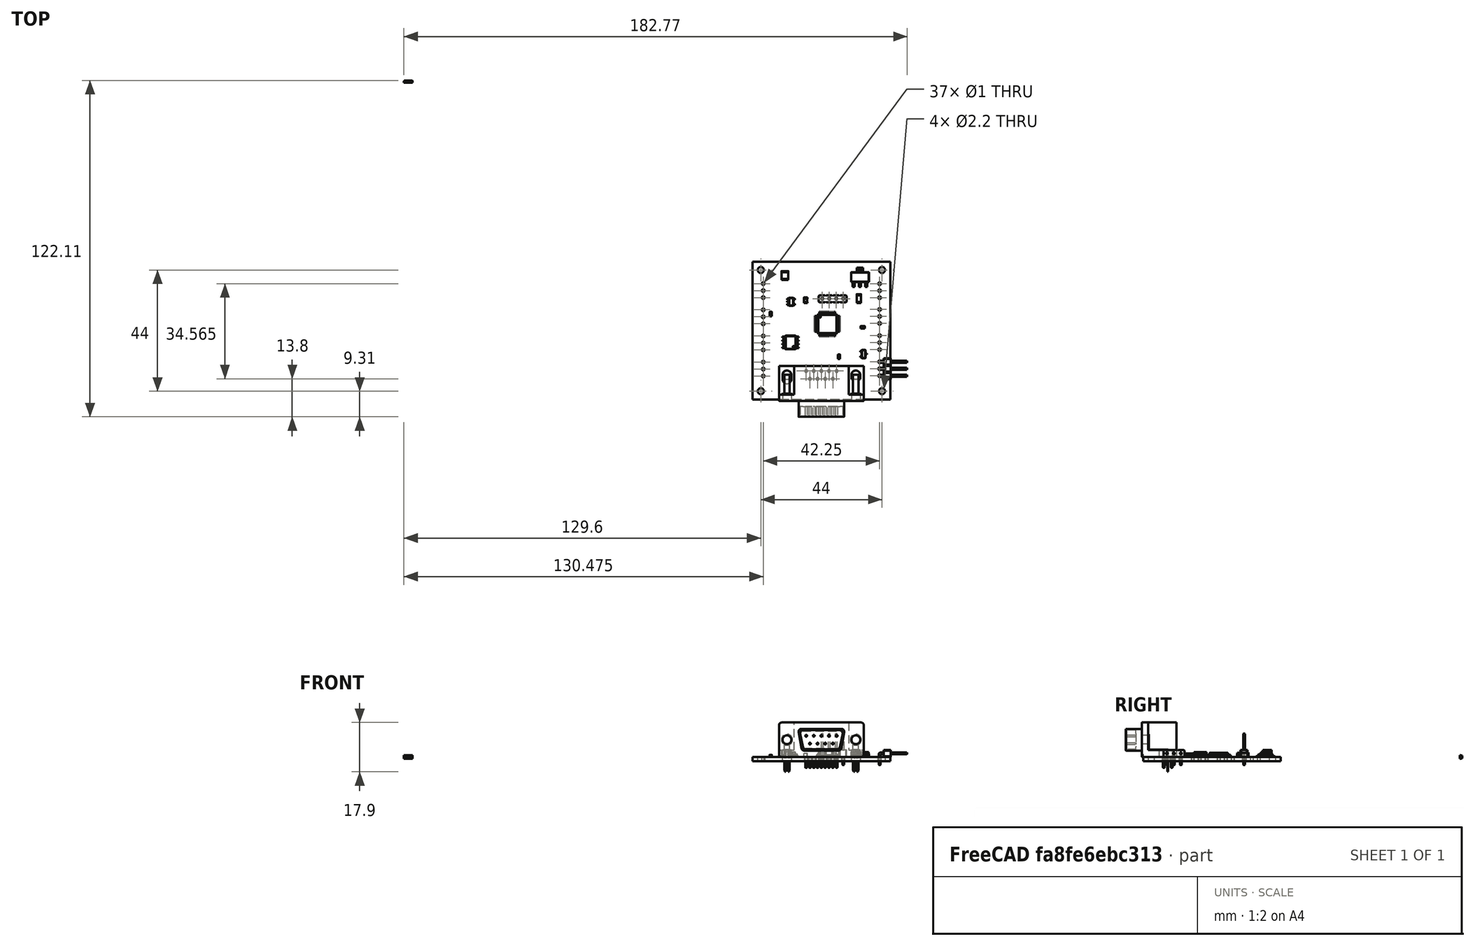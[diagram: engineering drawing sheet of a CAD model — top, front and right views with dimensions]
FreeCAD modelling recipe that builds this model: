
FCSTD DOCUMENT  (FreeCAD 0.20R29603 (Git))
Label: DGT-01
License: All rights reserved
LicenseURL: http://en.wikipedia.org/wiki/All_rights_reserved
objects: App::Link×55, Part::Feature×30, App::Part×6, PartDesign::CoordinateSystem×1, Sketcher::SketchObject×1
note: 32 computed .brp shape members not serialized (recipe doc carries the construction recipe); baked Part::Feature solids carry a one-line shape summary decoded from their .brp

FEATURE [PartDesign::CoordinateSystem] Local_CS_42b7
  AttacherType = Attacher::AttachEngine3D
  MapMode = 2
  Support = -> [X_Axis001]
FEATURE [Part::Feature] Pcb_42b7
  shape: bbox 50 x 50 x 1.6 mm, 49 faces (baked)
FEATURE [Sketcher::SketchObject] PCB_Sketch_42b7
  FullyConstrained = false
  sketch-geometry (4):
    g0: LineSegment StartX=125 StartY=-65.045 StartZ=0 EndX=175 EndY=-65.045 EndZ=0
    g1: LineSegment StartX=175 StartY=-65.045 StartZ=0 EndX=175 EndY=-115.045 EndZ=0
    g2: LineSegment StartX=175 StartY=-115.045 StartZ=0 EndX=125 EndY=-115.045 EndZ=0
    g3: LineSegment StartX=125 StartY=-115.045 StartZ=0 EndX=125 EndY=-65.045 EndZ=0
  constraints (4):
    c: Coincident(g2,g3)
    c: Coincident(g0,g3)
    c: Coincident(g1,g2)
    c: Coincident(g0,g1)
FEATURE [Part::Feature] Shape  label="R19_R_0603_1608Metric_04b1a8448a37"
  Placement = pos=(165,-88.8,0) rot=(0,0,1;0rad)
  shape: bbox 1.6 x 0.8 x 0.45 mm, 26 faces (baked)
FEATURE [Part::Feature] Shape001  label="C23_C_0603_1608Metric_67e658bcb3e9"
  Placement = pos=(131.6,-84,0) rot=(0,0,1;1.5708rad)
  shape: bbox 0.8 x 1.6 x 0.8 mm, 28 faces (baked)
FEATURE [Part::Feature] Shape002  label="J6_PinHeader_1x03_P254mm_Horizontal_46c90c8bffad"
  Placement = pos=(171.125,-101.32,0) rot=(0,0,1;0rad)
  shape: bbox 10.36 x 7.62 x 5.54 mm, 85 faces (baked)
FEATURE [App::Link] R19_R_0603_1608Metric_04b1a8448a37_ln_  label="R11_R_0603_1608Metric_9044ff0b4708"
  LinkPlacement = pos=(137.1,-99.825,0) rot=(0,0,1;1.5708rad)
  LinkedObject = -> Shape
  Placement = pos=(137.1,-99.825,0) rot=(0,0,1;1.5708rad)
FEATURE [App::Link] C23_C_0603_1608Metric_67e658bcb3e9_ln_  label="C17_C_0603_1608Metric_e9f00e3af137"
  LinkPlacement = pos=(168.4,-77.2,0) rot=(0,0,-1;1.5708rad)
  LinkedObject = -> Shape001
  Placement = pos=(168.4,-77.2,0) rot=(0,0,-1;1.5708rad)
FEATURE [App::Link] R19_R_0603_1608Metric_04b1a8448a37_ln_001  label="R6_R_0603_1608Metric_8a343aae5cf4"
  LinkPlacement = pos=(135.75,-74.75,0) rot=(0,0,-1;1.5708rad)
  LinkedObject = -> Shape
  Placement = pos=(135.75,-74.75,0) rot=(0,0,-1;1.5708rad)
FEATURE [App::Link] R19_R_0603_1608Metric_04b1a8448a37_ln_002  label="R10_R_0603_1608Metric_1eee93c9d580"
  LinkPlacement = pos=(135.1,-99.8,0) rot=(0,0,1;1.5708rad)
  LinkedObject = -> Shape
  Placement = pos=(135.1,-99.8,0) rot=(0,0,1;1.5708rad)
FEATURE [App::Link] R19_R_0603_1608Metric_04b1a8448a37_ln_003  label="R9_R_0603_1608Metric_2fc7657f437f"
  LinkPlacement = pos=(135.05,-77.15,0) rot=(0,0,1;0rad)
  LinkedObject = -> Shape
  Placement = pos=(135.05,-77.15,0) rot=(0,0,1;0rad)
FEATURE [App::Link] R19_R_0603_1608Metric_04b1a8448a37_ln_004  label="R7_R_0603_1608Metric_9dc4eea49bad"
  LinkPlacement = pos=(134,-79.5,0) rot=(0,0,1;1.5708rad)
  LinkedObject = -> Shape
  Placement = pos=(134,-79.5,0) rot=(0,0,1;1.5708rad)
FEATURE [App::Link] R19_R_0603_1608Metric_04b1a8448a37_ln_005  label="R23_R_0603_1608Metric_3db64d0de241"
  LinkPlacement = pos=(134.75,-85.1,0) rot=(0,0,1;3.14159rad)
  LinkedObject = -> Shape
  Placement = pos=(134.75,-85.1,0) rot=(0,0,1;3.14159rad)
FEATURE [App::Link] C23_C_0603_1608Metric_67e658bcb3e9_ln_001  label="C24_C_0603_1608Metric_34b0098a20eb"
  LinkPlacement = pos=(131.6,-74.4,0) rot=(0,0,1;1.5708rad)
  LinkedObject = -> Shape001
  Placement = pos=(131.6,-74.4,0) rot=(0,0,1;1.5708rad)
FEATURE [App::Link] R19_R_0603_1608Metric_04b1a8448a37_ln_006  label="R25_R_0603_1608Metric_28c4134f9de7"
  LinkPlacement = pos=(158.4,-99.5,0) rot=(0,0,1;1.5708rad)
  LinkedObject = -> Shape
  Placement = pos=(158.4,-99.5,0) rot=(0,0,1;1.5708rad)
FEATURE [App::Link] R19_R_0603_1608Metric_04b1a8448a37_ln_007  label="R26_R_0603_1608Metric_d651e4126f96"
  LinkPlacement = pos=(160.8,-98.4,0) rot=(0,0,-1;1.5708rad)
  LinkedObject = -> Shape
  Placement = pos=(160.8,-98.4,0) rot=(0,0,-1;1.5708rad)
FEATURE [Part::Feature] Shape003  label="U2_SOT_223_728849c4b83c"
  Placement = pos=(164,-70.6,0) rot=(0,0,1;1.5708rad)
  shape: bbox 6.5 x 7 x 1.7 mm, 78 faces (baked)
FEATURE [App::Link] J6_PinHeader_1x03_P254mm_Horizontal_46c90c8bffad_ln_  label="J7_PinHeader_1x03_P254mm_Horizontal_8abe0d3a7f01"
  LinkPlacement = pos=(128.875,-106.525,0) rot=(0,0,1;3.14159rad)
  LinkedObject = -> Shape002
  Placement = pos=(128.875,-106.525,0) rot=(0,0,1;3.14159rad)
FEATURE [App::Link] R19_R_0603_1608Metric_04b1a8448a37_ln_008  label="R16_R_0603_1608Metric_dfdb8e1241b6"
  LinkPlacement = pos=(146.25,-79.25,0) rot=(0,0,-1;1.5708rad)
  LinkedObject = -> Shape
  Placement = pos=(146.25,-79.25,0) rot=(0,0,-1;1.5708rad)
FEATURE [Part::Feature] Shape004  label="Q1_SOT_23_c58b233a5087"
  Placement = pos=(165.3,-98.5,0) rot=(0,0,1;0rad)
  shape: bbox 2.5 x 3 x 1.2 mm, 76 faces (baked)
FEATURE [Part::Feature] Part__Feature  label="CSTNE8M00GH5C000R0"
  shape: bbox 3 x 0.3 x 1.1 mm, 18 faces (baked)
FEATURE [Part::Feature] Part__Feature001  label="CSTNE8M00GH5C000R001"
  shape: bbox 0.2 x 0.5 x 1.3 mm, 6 faces (baked)
FEATURE [Part::Feature] Part__Feature002  label="CSTNE8M00GH5C000R002"
  shape: bbox 0.2 x 0.5 x 1.3 mm, 6 faces (baked)
FEATURE [Part::Feature] Part__Feature003  label="CSTNE8M00GH5C000R003"
  shape: bbox 0.4 x 0.5 x 1.3 mm, 6 faces (baked)
FEATURE [Part::Feature] Part__Feature004  label="CSTNE8M00GH5C000R004"
  shape: bbox 0.4 x 0.5 x 1.3 mm, 6 faces (baked)
FEATURE [Part::Feature] Part__Feature005  label="CSTNE8M00GH5C000R005"
  shape: bbox 0.4 x 0.45 x 1.3 mm, 6 faces (baked)
FEATURE [Part::Feature] Part__Feature006  label="CSTNE8M00GH5C000R006"
  shape: bbox 2 x 0.5 x 1.3 mm, 10 faces (baked)
FEATURE [App::Part] CSTNE8M00GH5C000R0  label="Y1_CSTNE8M00GH5C000R007_5459dfa8324f"
  Group = -> [Part__Feature,Part__Feature001,Part__Feature002,Part__Feature003,Part__Feature004,Part__Feature005,Part__Feature006]
  Origin = -> Origin008
  Placement = pos=(145.3,-88.1,0) rot=(0.57735,-0.57735,-0.57735;2.0944rad)
FEATURE [Part::Feature] Shape005  label="C7_C_1206_3216Metric_4a6abfde341f"
  Placement = pos=(163.6,-78.4,0) rot=(0,0,1;1.5708rad)
  shape: bbox 1.6 x 3.2 x 1.6 mm, 28 faces (baked)
FEATURE [Part::Feature] Shape006  label="D2_LED_0603_1608Metric_9a2b872fa988"
  Placement = pos=(156.4,-99.5,0) rot=(0,0,1;1.5708rad)
  shape: bbox 0.8 x 1.6 x 1.1 mm, 50 faces (baked)
FEATURE [App::Link] U2_SOT_223_728849c4b83c_ln_  label="U1_SOT_223_b2e5ecc5a7cd"
  LinkPlacement = pos=(145.3,-70.6,0) rot=(0,0,1;1.5708rad)
  LinkedObject = -> Shape003
  Placement = pos=(145.3,-70.6,0) rot=(0,0,1;1.5708rad)
FEATURE [App::Link] C23_C_0603_1608Metric_67e658bcb3e9_ln_002  label="C9_C_0603_1608Metric_85e27d3c77db"
  LinkPlacement = pos=(139.1,-76.55,0) rot=(0,0,1;3.14159rad)
  LinkedObject = -> Shape001
  Placement = pos=(139.1,-76.55,0) rot=(0,0,1;3.14159rad)
FEATURE [App::Link] C23_C_0603_1608Metric_67e658bcb3e9_ln_003  label="C19_C_0603_1608Metric_8a213d718a65"
  LinkPlacement = pos=(168.4,-95.6,0) rot=(0,0,-1;1.5708rad)
  LinkedObject = -> Shape001
  Placement = pos=(168.4,-95.6,0) rot=(0,0,-1;1.5708rad)
FEATURE [App::Link] C23_C_0603_1608Metric_67e658bcb3e9_ln_004  label="C6_C_0603_1608Metric_23fe59c1562e"
  LinkPlacement = pos=(135.8,-79.5,0) rot=(0,0,1;1.5708rad)
  LinkedObject = -> Shape001
  Placement = pos=(135.8,-79.5,0) rot=(0,0,1;1.5708rad)
FEATURE [App::Link] R19_R_0603_1608Metric_04b1a8448a37_ln_009  label="R13_R_0603_1608Metric_7d51a89331da"
  LinkPlacement = pos=(142.25,-79.25,0) rot=(0,0,1;1.5708rad)
  LinkedObject = -> Shape
  Placement = pos=(142.25,-79.25,0) rot=(0,0,1;1.5708rad)
FEATURE [App::Link] R19_R_0603_1608Metric_04b1a8448a37_ln_010  label="R12_R_0603_1608Metric_22d4fa4ee4f3"
  LinkPlacement = pos=(158.5,-82.8,0) rot=(0,0,-1;1.5708rad)
  LinkedObject = -> Shape
  Placement = pos=(158.5,-82.8,0) rot=(0,0,-1;1.5708rad)
FEATURE [App::Link] J6_PinHeader_1x03_P254mm_Horizontal_46c90c8bffad_ln_001  label="J5_PinHeader_1x03_P254mm_Horizontal_be8940a4bbb2"
  LinkPlacement = pos=(171.125,-91.82,0) rot=(0,0,1;0rad)
  LinkedObject = -> Shape002
  Placement = pos=(171.125,-91.82,0) rot=(0,0,1;0rad)
FEATURE [Part::Feature] Shape007  label="J2_PinHeader_1x04_P254mm_Vertical_68b31ef03787"
  Placement = pos=(157.9,-78.4,0) rot=(0,0,-1;1.5708rad)
  shape: bbox 10.16 x 2.54 x 11.54 mm, 100 faces (baked)
FEATURE [App::Link] R19_R_0603_1608Metric_04b1a8448a37_ln_011  label="R5_R_0603_1608Metric_b431cbdac7d4"
  LinkPlacement = pos=(154.1,-99.475,0) rot=(0,0,1;1.5708rad)
  LinkedObject = -> Shape
  Placement = pos=(154.1,-99.475,0) rot=(0,0,1;1.5708rad)
FEATURE [App::Link] C23_C_0603_1608Metric_67e658bcb3e9_ln_005  label="C18_C_0603_1608Metric_4ebd43163757"
  LinkPlacement = pos=(168.4,-86.2,0) rot=(0,0,-1;1.5708rad)
  LinkedObject = -> Shape001
  Placement = pos=(168.4,-86.2,0) rot=(0,0,-1;1.5708rad)
FEATURE [App::Link] R19_R_0603_1608Metric_04b1a8448a37_ln_012  label="R2_R_0603_1608Metric_b5563379a259"
  LinkPlacement = pos=(149,-99.475,0) rot=(0,0,1;1.5708rad)
  LinkedObject = -> Shape
  Placement = pos=(149,-99.475,0) rot=(0,0,1;1.5708rad)
FEATURE [App::Link] C23_C_0603_1608Metric_67e658bcb3e9_ln_006  label="C21_C_0603_1608Metric_43905a34d840"
  LinkPlacement = pos=(131.575,-103,0) rot=(0,0,1;1.5708rad)
  LinkedObject = -> Shape001
  Placement = pos=(131.575,-103,0) rot=(0,0,1;1.5708rad)
FEATURE [App::Link] R19_R_0603_1608Metric_04b1a8448a37_ln_013  label="R3_R_0603_1608Metric_477e2f9ed346"
  LinkPlacement = pos=(150.7,-99.475,0) rot=(0,0,1;1.5708rad)
  LinkedObject = -> Shape
  Placement = pos=(150.7,-99.475,0) rot=(0,0,1;1.5708rad)
FEATURE [App::Link] R19_R_0603_1608Metric_04b1a8448a37_ln_014  label="R17_R_0603_1608Metric_315bb9e28f19"
  LinkPlacement = pos=(165,-85.3,0) rot=(0,0,1;0rad)
  LinkedObject = -> Shape
  Placement = pos=(165,-85.3,0) rot=(0,0,1;0rad)
FEATURE [App::Link] R19_R_0603_1608Metric_04b1a8448a37_ln_015  label="R22_R_0603_1608Metric_b586d086ac36"
  LinkPlacement = pos=(134.75,-87.1,0) rot=(0,0,1;3.14159rad)
  LinkedObject = -> Shape
  Placement = pos=(134.75,-87.1,0) rot=(0,0,1;3.14159rad)
FEATURE [App::Link] R19_R_0603_1608Metric_04b1a8448a37_ln_016  label="R18_R_0603_1608Metric_15c85b268854"
  LinkPlacement = pos=(165,-87.1,0) rot=(0,0,1;0rad)
  LinkedObject = -> Shape
  Placement = pos=(165,-87.1,0) rot=(0,0,1;0rad)
FEATURE [App::Link] R19_R_0603_1608Metric_04b1a8448a37_ln_017  label="R21_R_0603_1608Metric_848edafc6296"
  LinkPlacement = pos=(134.75,-89,0) rot=(0,0,1;3.14159rad)
  LinkedObject = -> Shape
  Placement = pos=(134.75,-89,0) rot=(0,0,1;3.14159rad)
FEATURE [Part::Feature] Shape008  label="U3_SOT_23_5_2c270eb65cb8"
  Placement = pos=(139,-79.5,0) rot=(0,0,1;0rad)
  shape: bbox 2.8 x 2.9 x 1.55 mm, 109 faces (baked)
FEATURE [App::Link] J6_PinHeader_1x03_P254mm_Horizontal_46c90c8bffad_ln_002  label="J10_PinHeader_1x03_P254mm_Horizontal_e4195cf57d88"
  LinkPlacement = pos=(128.875,-78.025,0) rot=(0,0,1;3.14159rad)
  LinkedObject = -> Shape002
  Placement = pos=(128.875,-78.025,0) rot=(0,0,1;3.14159rad)
FEATURE [Part::Feature] Shape009  label="C11_C_0805_2012Metric_1688cc946903"
  Placement = pos=(144.25,-79,0) rot=(0,0,1;1.5708rad)
  shape: bbox 1.25 x 2 x 1.25 mm, 28 faces (baked)
FEATURE [App::Link] Q1_SOT_23_c58b233a5087_ln_  label="D1_SOT_23_b0d5b012e837"
  LinkPlacement = pos=(154.9,-73,0) rot=(0,0,1;0rad)
  LinkedObject = -> Shape004
  Placement = pos=(154.9,-73,0) rot=(0,0,1;0rad)
FEATURE [Part::Feature] Shape010  label="J1_DSUB-9_Male_Horizontal_P2.77x2.84mm_EdgePinOffset7.70mm_Housed_
MountingHolesOffset9.12mm_90076e21dd48"
  Placement = pos=(144.45,-104.67,0) rot=(0,0,1;0rad)
  shape: bbox 30.96 x 18.44 x 17.98 mm, 181 faces (baked)
FEATURE [App::Link] C23_C_0603_1608Metric_67e658bcb3e9_ln_007  label="C15_C_0603_1608Metric_995048d5ef05"
  LinkPlacement = pos=(145.25,-85.25,0) rot=(0,0,1;3.14159rad)
  LinkedObject = -> Shape001
  Placement = pos=(145.25,-85.25,0) rot=(0,0,1;3.14159rad)
FEATURE [App::Link] R19_R_0603_1608Metric_04b1a8448a37_ln_018  label="R8_R_0603_1608Metric_37551f048aa7"
  LinkPlacement = pos=(143.1,-99.9,0) rot=(0,0,1;1.5708rad)
  LinkedObject = -> Shape
  Placement = pos=(143.1,-99.9,0) rot=(0,0,1;1.5708rad)
FEATURE [App::Link] R19_R_0603_1608Metric_04b1a8448a37_ln_019  label="R24_R_0603_1608Metric_4e0f9286edfd"
  LinkPlacement = pos=(134.75,-83.2,0) rot=(0,0,1;3.14159rad)
  LinkedObject = -> Shape
  Placement = pos=(134.75,-83.2,0) rot=(0,0,1;3.14159rad)
FEATURE [App::Link] C23_C_0603_1608Metric_67e658bcb3e9_ln_008  label="C10_C_0603_1608Metric_e1d64a5043b0"
  LinkPlacement = pos=(134.2,-94.2,0) rot=(0,0,1;1.5708rad)
  LinkedObject = -> Shape001
  Placement = pos=(134.2,-94.2,0) rot=(0,0,1;1.5708rad)
FEATURE [App::Link] C11_C_0805_2012Metric_1688cc946903_ln_  label="C2_C_0805_2012Metric_3e8ded921b53"
  LinkPlacement = pos=(139.75,-69.5,0) rot=(0,0,-1;1.5708rad)
  LinkedObject = -> Shape009
  Placement = pos=(139.75,-69.5,0) rot=(0,0,-1;1.5708rad)
FEATURE [App::Link] R19_R_0603_1608Metric_04b1a8448a37_ln_020  label="R4_R_0603_1608Metric_20c0023253bd"
  LinkPlacement = pos=(152.4,-99.475,0) rot=(0,0,1;1.5708rad)
  LinkedObject = -> Shape
  Placement = pos=(152.4,-99.475,0) rot=(0,0,1;1.5708rad)
FEATURE [App::Link] J6_PinHeader_1x03_P254mm_Horizontal_46c90c8bffad_ln_003  label="J3_PinHeader_1x03_P254mm_Horizontal_a15aa3efdf36"
  LinkPlacement = pos=(171.125,-72.975,0) rot=(0,0,1;0rad)
  LinkedObject = -> Shape002
  Placement = pos=(171.125,-72.975,0) rot=(0,0,1;0rad)
FEATURE [Part::Feature] Shape011  label="U4_SOIC_8_39x49mm_P127mm_61171556ec97"
  Placement = pos=(138.8,-94.3,0) rot=(0,0,1;3.14159rad)
  shape: bbox 6 x 4.9 x 1.75 mm, 156 faces (baked)
FEATURE [App::Link] C23_C_0603_1608Metric_67e658bcb3e9_ln_009  label="C22_C_0603_1608Metric_b0bb3c3e1635"
  LinkPlacement = pos=(131.55,-93.6,0) rot=(0,0,1;1.5708rad)
  LinkedObject = -> Shape001
  Placement = pos=(131.55,-93.6,0) rot=(0,0,1;1.5708rad)
FEATURE [App::Link] R19_R_0603_1608Metric_04b1a8448a37_ln_021  label="R27_R_0603_1608Metric_cb8b4c943f02"
  LinkPlacement = pos=(162.5,-98.4,0) rot=(0,0,-1;1.5708rad)
  LinkedObject = -> Shape
  Placement = pos=(162.5,-98.4,0) rot=(0,0,-1;1.5708rad)
FEATURE [App::Link] C23_C_0603_1608Metric_67e658bcb3e9_ln_010  label="C20_C_0603_1608Metric_f752ad345f4a"
  LinkPlacement = pos=(168.275,-105.2,0) rot=(0,0,-1;1.5708rad)
  LinkedObject = -> Shape001
  Placement = pos=(168.275,-105.2,0) rot=(0,0,-1;1.5708rad)
FEATURE [App::Link] J6_PinHeader_1x03_P254mm_Horizontal_46c90c8bffad_ln_004  label="J9_PinHeader_1x03_P254mm_Horizontal_09e8b1dd86cf"
  LinkPlacement = pos=(128.875,-87.525,0) rot=(0,0,1;3.14159rad)
  LinkedObject = -> Shape002
  Placement = pos=(128.875,-87.525,0) rot=(0,0,1;3.14159rad)
FEATURE [App::Link] J6_PinHeader_1x03_P254mm_Horizontal_46c90c8bffad_ln_005  label="J8_PinHeader_1x03_P254mm_Horizontal_6b37209e496f"
  LinkPlacement = pos=(128.875,-97.025,0) rot=(0,0,1;3.14159rad)
  LinkedObject = -> Shape002
  Placement = pos=(128.875,-97.025,0) rot=(0,0,1;3.14159rad)
FEATURE [App::Link] R19_R_0603_1608Metric_04b1a8448a37_ln_022  label="R20_R_0603_1608Metric_631bd143e91f"
  LinkPlacement = pos=(165,-83.5,0) rot=(0,0,1;0rad)
  LinkedObject = -> Shape
  Placement = pos=(165,-83.5,0) rot=(0,0,1;0rad)
FEATURE [App::Link] J6_PinHeader_1x03_P254mm_Horizontal_46c90c8bffad_ln_006  label="J4_PinHeader_1x03_P254mm_Horizontal_bc5e5132952c"
  LinkPlacement = pos=(171.125,-82.32,0) rot=(0,0,1;0rad)
  LinkedObject = -> Shape002
  Placement = pos=(171.125,-82.32,0) rot=(0,0,1;0rad)
FEATURE [App::Link] C23_C_0603_1608Metric_67e658bcb3e9_ln_011  label="C3_C_0603_1608Metric_9308765661dd"
  LinkPlacement = pos=(160.6,-79.2,0) rot=(0,0,-1;1.5708rad)
  LinkedObject = -> Shape001
  Placement = pos=(160.6,-79.2,0) rot=(0,0,-1;1.5708rad)
FEATURE [App::Link] C7_C_1206_3216Metric_4a6abfde341f_ln_  label="C5_C_1206_3216Metric_b4d6b5bd6ad1"
  LinkPlacement = pos=(158.5,-73,0) rot=(0,0,-1;1.5708rad)
  LinkedObject = -> Shape005
  Placement = pos=(158.5,-73,0) rot=(0,0,-1;1.5708rad)
FEATURE [App::Link] C23_C_0603_1608Metric_67e658bcb3e9_ln_012  label="C8_C_0603_1608Metric_30e2a4bc65d4"
  LinkPlacement = pos=(165.9,-77.8,0) rot=(0,0,1;1.5708rad)
  LinkedObject = -> Shape001
  Placement = pos=(165.9,-77.8,0) rot=(0,0,1;1.5708rad)
FEATURE [Part::Feature] Shape012  label="U5_LQFP_48_7x7mm_P05mm_9a45da788053"
  Placement = pos=(152.13,-87.6,0) rot=(0,0,1;0rad)
  shape: bbox 9 x 9 x 1.5 mm, 764 faces (baked)
FEATURE [App::Link] C7_C_1206_3216Metric_4a6abfde341f_ln_001  label="C4_C_1206_3216Metric_1186cc1c97c4"
  LinkPlacement = pos=(151.2,-72.7,0) rot=(0,0,-1;1.5708rad)
  LinkedObject = -> Shape005
  Placement = pos=(151.2,-72.7,0) rot=(0,0,-1;1.5708rad)
FEATURE [Part::Feature] Shape013  label="C1_C_1210_3225Metric_febb3d8b4366"
  Placement = pos=(136.75,-70,0) rot=(0,0,-1;1.5708rad)
  shape: bbox 2.5 x 3.2 x 2.5 mm, 28 faces (baked)
FEATURE [App::Link] R19_R_0603_1608Metric_04b1a8448a37_ln_023  label="R1_R_0603_1608Metric_a0c4ad1bf538"
  LinkPlacement = pos=(147.3,-99.475,0) rot=(0,0,1;1.5708rad)
  LinkedObject = -> Shape
  Placement = pos=(147.3,-99.475,0) rot=(0,0,1;1.5708rad)
FEATURE [App::Part] Top_42b7
  Group = -> [Shape,Shape001,Shape002,R19_R_0603_1608Metric_04b1a8448a37_ln_,C23_C_0603_1608Metric_67e658bcb3e9_ln_,R19_R_0603_1608Metric_04b1a8448a37_ln_001,R19_R_0603_1608Metric_04b1a8448a37_ln_002,R19_R_0603_1608Metric_04b1a8448a37_ln_003,R19_R_0603_1608Metric_04b1a8448a37_ln_004,R19_R_0603_1608Metric_04b1a8448a37_ln_005,C23_C_0603_1608Metric_67e658bcb3e9_ln_001,R19_R_0603_1608Metric_04b1a8448a37_ln_006,+52 more]
  Origin = -> Origin003
FEATURE [App::Link] C23_C_0603_1608Metric_67e658bcb3e9_ln_013  label="C13_C_0603_1608Metric_e6bd0ca13b07"
  LinkPlacement = pos=(154.5,-85.9,-1.6) rot=(0.707107,-0.707107,0;3.14159rad)
  LinkedObject = -> Shape001
  Placement = pos=(154.5,-85.9,-1.6) rot=(0.707107,-0.707107,0;3.14159rad)
FEATURE [App::Link] C23_C_0603_1608Metric_67e658bcb3e9_ln_014  label="C12_C_0603_1608Metric_574b1417282d"
  LinkPlacement = pos=(154,-90,-1.6) rot=(0,1,0;3.14159rad)
  LinkedObject = -> Shape001
  Placement = pos=(154,-90,-1.6) rot=(0,1,0;3.14159rad)
FEATURE [App::Link] R19_R_0603_1608Metric_04b1a8448a37_ln_024  label="R15_R_0603_1608Metric_1764a2733b1e"
  LinkPlacement = pos=(152.5,-88.25,-1.6) rot=(1,0,0;3.14159rad)
  LinkedObject = -> Shape
  Placement = pos=(152.5,-88.25,-1.6) rot=(1,0,0;3.14159rad)
FEATURE [App::Link] C23_C_0603_1608Metric_67e658bcb3e9_ln_015  label="C14_C_0603_1608Metric_81392f8e2ded"
  LinkPlacement = pos=(149.8,-86,-1.6) rot=(0.707107,-0.707107,0;3.14159rad)
  LinkedObject = -> Shape001
  Placement = pos=(149.8,-86,-1.6) rot=(0.707107,-0.707107,0;3.14159rad)
FEATURE [App::Link] R19_R_0603_1608Metric_04b1a8448a37_ln_025  label="R14_R_0603_1608Metric_aa714409e06c"
  LinkPlacement = pos=(152.15,-85.5,-1.6) rot=(0,1,0;3.14159rad)
  LinkedObject = -> Shape
  Placement = pos=(152.15,-85.5,-1.6) rot=(0,1,0;3.14159rad)
FEATURE [App::Link] C23_C_0603_1608Metric_67e658bcb3e9_ln_016  label="C16_C_0603_1608Metric_0a61d1811865"
  LinkPlacement = pos=(150,-89.3,-1.6) rot=(0.707107,0.707107,0;3.14159rad)
  LinkedObject = -> Shape001
  Placement = pos=(150,-89.3,-1.6) rot=(0.707107,0.707107,0;3.14159rad)
FEATURE [App::Part] Bot_42b7
  Group = -> [C23_C_0603_1608Metric_67e658bcb3e9_ln_013,C23_C_0603_1608Metric_67e658bcb3e9_ln_014,R19_R_0603_1608Metric_04b1a8448a37_ln_024,C23_C_0603_1608Metric_67e658bcb3e9_ln_015,R19_R_0603_1608Metric_04b1a8448a37_ln_025,C23_C_0603_1608Metric_67e658bcb3e9_ln_016]
  Origin = -> Origin004
FEATURE [App::Part] Step_Models_42b7
  Group = -> [Top_42b7,Bot_42b7]
  Origin = -> Origin002
FEATURE [Part::Feature] pads_area069001  label="topPads_42b7"
  Placement = pos=(0,0,0.02) rot=(0,0,1;0rad)
  shape: bbox 43.95 x 41.86 x 2e-07 mm, 276 faces, 0 solids (baked)
FEATURE [Part::Feature] Shape014001  label="topTracks_42b7"
  Placement = pos=(0,0,0.01) rot=(0,0,1;0rad)
  shape: bbox 46.94 x 39.94 x 2e-07 mm, 99 faces, 0 solids (baked)
FEATURE [Part::Feature] zones_area001  label="topZones_42b7"
  Placement = pos=(0,0,0.01) rot=(0,0,1;0rad)
  shape: bbox 26.75 x 6.905 x 2e-07 mm, 2 faces, 0 solids (baked)
FEATURE [Part::Feature] pads_area069027001  label="botPads_42b7"
  Placement = pos=(0,0,-1.62) rot=(0,0,1;0rad)
  shape: bbox 43.95 x 45.18 x 2e-07 mm, 137 faces, 0 solids (baked)
FEATURE [Part::Feature] Shape014002001  label="botTracks_42b7"
  Placement = pos=(0,0,-1.61) rot=(0,0,1;0rad)
  shape: bbox 27.19 x 34.3 x 2e-07 mm, 28 faces, 0 solids (baked)
FEATURE [Part::Feature] zones_area002001  label="botZones_42b7"
  Placement = pos=(0,0,-1.61) rot=(0,0,1;0rad)
  shape: bbox 48.05 x 48.05 x 2e-07 mm, 1 faces, 0 solids (baked)
FEATURE [Part::Feature] botSilks_df42
  Placement = pos=(0,0,-1.67) rot=(0,0,1;0rad)
  shape: bbox 47.95 x 47.34 x 2e-07 mm, 206 faces, 0 solids (baked)
FEATURE [Part::Feature] topSilks_d296
  Placement = pos=(0,0,0.07) rot=(0,0,1;0rad)
  shape: bbox 49.57 x 47.62 x 2e-07 mm, 302 faces, 0 solids (baked)
FEATURE [App::Part] Board_Geoms_42b7
  Group = -> [Pcb_42b7,PCB_Sketch_42b7,pads_area069001,Shape014001,zones_area001,pads_area069027001,Shape014002001,zones_area002001,botSilks_df42,topSilks_d296]
  Origin = -> Origin
FEATURE [App::Part] Board_42b7  label="DGT-01"
  Group = -> [Local_CS_42b7,Board_Geoms_42b7,Step_Models_42b7]
  Origin = -> Origin001
